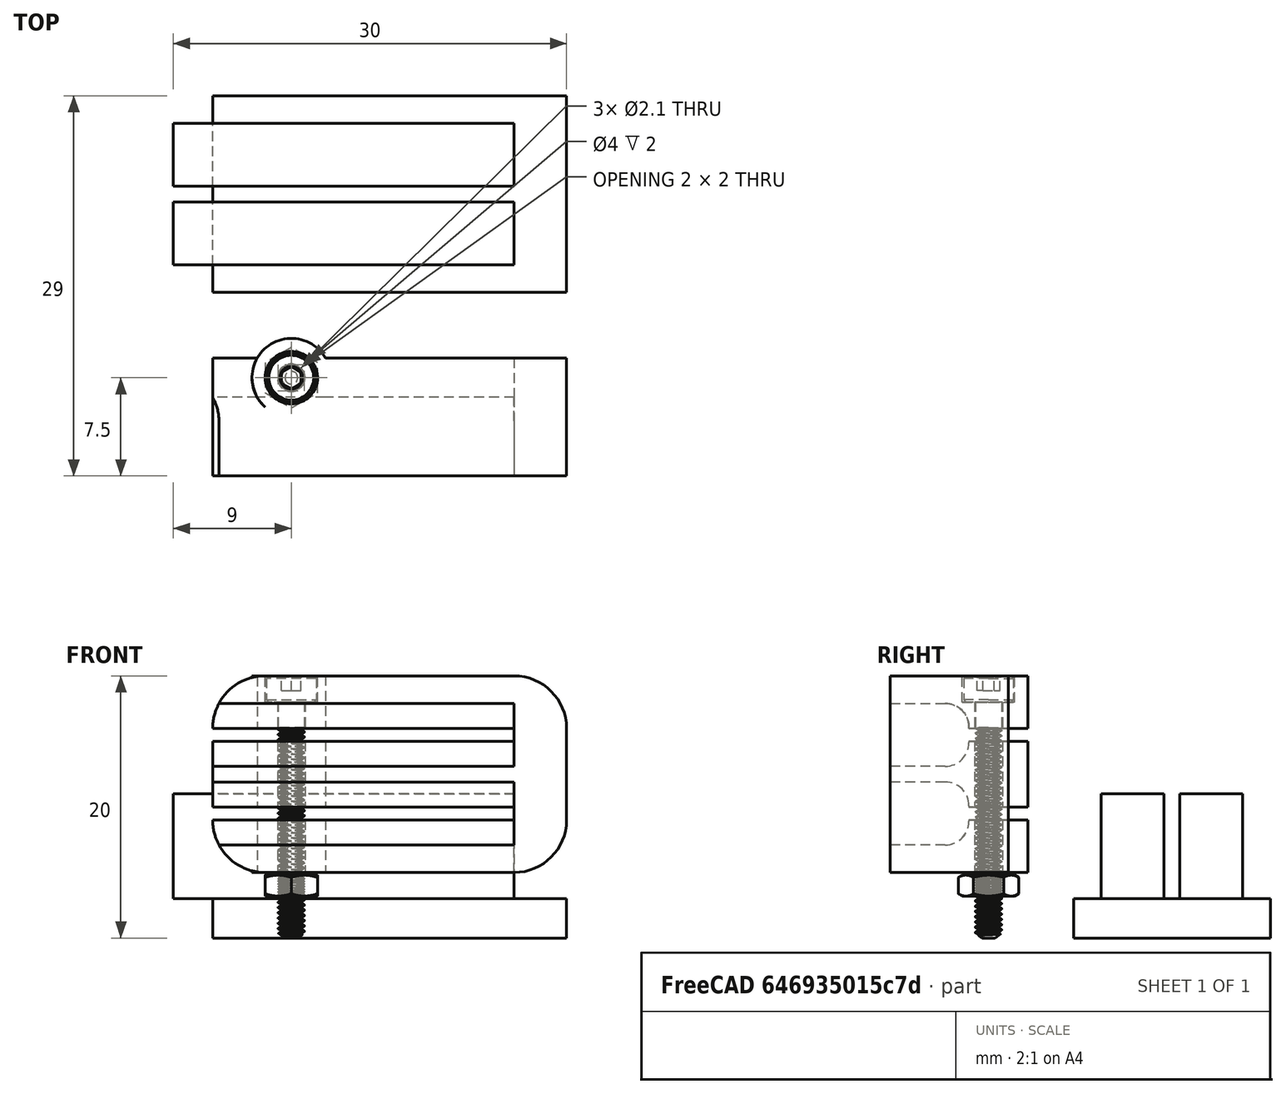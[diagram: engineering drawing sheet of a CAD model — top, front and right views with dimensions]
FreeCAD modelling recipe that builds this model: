
FCSTD DOCUMENT  (FreeCAD 0.16R6705 (Git))
Label: IntanHeadstageSpacer_v2
License: All rights reserved
LicenseURL: http://en.wikipedia.org/wiki/All_rights_reserved
objects: Part::Extrusion×12, Part::Part2DObjectPython×10, Part::Cut×4, Part::Cylinder×3, Part::MultiFuse×3, Part::Fillet×2, Part::Feature×2
note: 36 computed .brp shape members not serialized (recipe doc carries the construction recipe); baked Part::Feature solids carry a one-line shape summary decoded from their .brp

FEATURE [Part::Part2DObjectPython] Rectangle  # Draft 2D object (typed FeaturePython)
  ChamferSize = 0
  Columns = 1
  FilletRadius = 0
  Height = -15
  Length = 27
  MakeFace = true
  Placement = pos=(-20,20,0) rot=(0,0,1;0rad)
  Rows = 1
FEATURE [Part::Extrusion] Extrude
  Base = -> Rectangle
  Dir = (0,0,9)
  Solid = true
FEATURE [Part::Extrusion] Extrude001
  Base = -> Rectangle
  Dir = (0,0,3)
  Solid = true
FEATURE [Part::Fillet] Fillet
  Base = -> Extrude
  Edges = 4 edges r=4: [Edge1,Edge2,Edge5,Edge8]
FEATURE [Part::Part2DObjectPython] Rectangle001  # Draft 2D object (typed FeaturePython)
  ChamferSize = 0
  Columns = 1
  FilletRadius = 0
  Height = 1
  Length = 26
  MakeFace = true
  Placement = pos=(-23,16,0) rot=(0,0,1;0rad)
  Rows = 1
FEATURE [Part::Extrusion] Extrude002
  Base = -> Rectangle001
  Dir = (0,0,-20)
  Placement = pos=(0,-1,10) rot=(0,0,1;0rad)
  Solid = true
FEATURE [Part::Part2DObjectPython] Rectangle002  # Draft 2D object (typed FeaturePython)
  ChamferSize = 0
  Columns = 1
  FilletRadius = 0
  Height = -1
  Length = 26
  MakeFace = true
  Placement = pos=(-23,10,0) rot=(0,0,1;0rad)
  Rows = 1
FEATURE [Part::Extrusion] Extrude004
  Base = -> Rectangle002
  Dir = (0,0,20)
  Placement = pos=(0,0,-4) rot=(0,0,1;0rad)
  Solid = true
FEATURE [Part::Part2DObjectPython] Rectangle003  # Draft 2D object (typed FeaturePython)
  ChamferSize = 0
  Columns = 1
  FilletRadius = 0
  Height = -1.4
  Length = 15
  MakeFace = true
  Placement = pos=(-13,22,0) rot=(0,0,1;0rad)
  Rows = 1
FEATURE [Part::Part2DObjectPython] Rectangle004  # Draft 2D object (typed FeaturePython)
  ChamferSize = 0
  Columns = 1
  FilletRadius = 0
  Height = 4.8
  Length = 26
  MakeFace = true
  Placement = pos=(-23,13.1,0) rot=(0,0,1;0rad)
  Rows = 1
FEATURE [Part::Extrusion] Extrude005
  Base = -> Rectangle004
  Dir = (0,0,-8)
  Placement = pos=(0,0,11) rot=(0,0,1;0rad)
  Solid = true
FEATURE [Part::Extrusion] Extrude006
  Base = -> Rectangle004
  Dir = (0,0,-8)
  Placement = pos=(0,0,11) rot=(0,0,1;0rad)
  Solid = true
FEATURE [Part::Part2DObjectPython] Rectangle005  # Draft 2D object (typed FeaturePython)
  ChamferSize = 0
  Columns = 1
  FilletRadius = 0
  Height = -4.8
  Length = 26
  MakeFace = true
  Placement = pos=(-23,11.9,0) rot=(0,0,1;0rad)
  Rows = 1
FEATURE [Part::Extrusion] Extrude007
  Base = -> Rectangle005
  Dir = (0,0,8)
  Placement = pos=(0,0,3) rot=(0,0,1;0rad)
  Solid = true
FEATURE [Part::Extrusion] Extrude008
  Base = -> Rectangle005
  Dir = (0,0,8)
  Placement = pos=(0,0,3) rot=(0,0,1;0rad)
  Solid = true
FEATURE [Part::Cylinder] Cylinder001
  Angle = 360
  Height = 15
  Placement = pos=(-14,20,1.5) rot=(1,0,0;1.5708rad)
  Radius = 3
FEATURE [Part::Cylinder] Cylinder
  Angle = 360
  Height = 20
  Placement = pos=(-14,21,1.5) rot=(1,0,0;1.5708rad)
  Radius = 1.05
FEATURE [Part::MultiFuse] Fusion
  Shapes = -> [Extrude002,Extrude005,Extrude004,Extrude008]
FEATURE [Part::Part2DObjectPython] Rectangle006  # Draft 2D object (typed FeaturePython)
  ChamferSize = 0
  Columns = 1
  FilletRadius = 0
  Height = 1
  Length = 26
  MakeFace = true
  Placement = pos=(-23,16,0) rot=(0,0,1;0rad)
  Rows = 1
FEATURE [Part::Extrusion] Extrude009
  Base = -> Rectangle006
  Dir = (0,0,-20)
  Placement = pos=(0,-1,10) rot=(0,0,1;0rad)
  Solid = true
FEATURE [Part::Part2DObjectPython] Rectangle007  # Draft 2D object (typed FeaturePython)
  ChamferSize = 0
  Columns = 1
  FilletRadius = 0
  Height = -1
  Length = 26
  MakeFace = true
  Placement = pos=(-23,10,0) rot=(0,0,1;0rad)
  Rows = 1
FEATURE [Part::Extrusion] Extrude010
  Base = -> Rectangle007
  Dir = (0,0,20)
  Placement = pos=(0,0,-4) rot=(0,0,1;0rad)
  Solid = true
FEATURE [Part::Part2DObjectPython] Rectangle008  # Draft 2D object (typed FeaturePython)
  ChamferSize = 0
  Columns = 1
  FilletRadius = 0
  Height = 4.8
  Length = 26
  MakeFace = true
  Placement = pos=(-23,13.1,0) rot=(0,0,1;0rad)
  Rows = 1
FEATURE [Part::Extrusion] Extrude011
  Base = -> Rectangle008
  Dir = (0,0,-8)
  Placement = pos=(0,0,11) rot=(0,0,1;0rad)
  Solid = true
FEATURE [Part::Part2DObjectPython] Rectangle009  # Draft 2D object (typed FeaturePython)
  ChamferSize = 0
  Columns = 1
  FilletRadius = 0
  Height = -4.8
  Length = 26
  MakeFace = true
  Placement = pos=(-23,11.9,0) rot=(0,0,1;0rad)
  Rows = 1
FEATURE [Part::Extrusion] Extrude012
  Base = -> Rectangle009
  Dir = (0,0,8)
  Placement = pos=(0,0,3) rot=(0,0,1;0rad)
  Solid = true
FEATURE [Part::MultiFuse] Fusion001
  Shapes = -> [Extrude009,Extrude011,Extrude010,Extrude012]
FEATURE [Part::Cut] Cut
  Base = -> Fillet
  Tool = -> Fusion
FEATURE [Part::Fillet] Fillet001
  Base = -> Cut
  Edges = 4 edges r=1.8: [Edge61,Edge64,Edge71,Edge73]
FEATURE [Part::Cut] Cut001
  Base = -> Cylinder001
  Tool = -> Fusion001
FEATURE [Part::MultiFuse] Fusion002
  Shapes = -> [Cut001,Fillet001]
FEATURE [Part::Cut] Cut002
  Base = -> Fusion002
  Placement = pos=(0,0,0) rot=(1,0,0;1.5708rad)
  Tool = -> Cylinder
FEATURE [Part::Cylinder] Cylinder002
  Angle = 360
  Height = 2
  Placement = pos=(-14,-1.5,18) rot=(0,0,1;0rad)
  Radius = 2
FEATURE [Part::Cut] Cut003
  Base = -> Cut002
  Tool = -> Cylinder002
FEATURE [Part::Feature] Part__Feature  label="91292A031"
  Placement = pos=(-14,-1.5,0) rot=(1,0,0;3.14159rad)
  shape: bbox 3.801 x 3.801 x 20.02 mm, 191 faces (baked)
FEATURE [Part::Feature] Part__Feature001  label="90591A265"
  Placement = pos=(-14,-1.5,4) rot=(0,0,1;0rad)
  shape: bbox 4.619 x 4.619 x 1.951 mm, 45 faces (baked)
